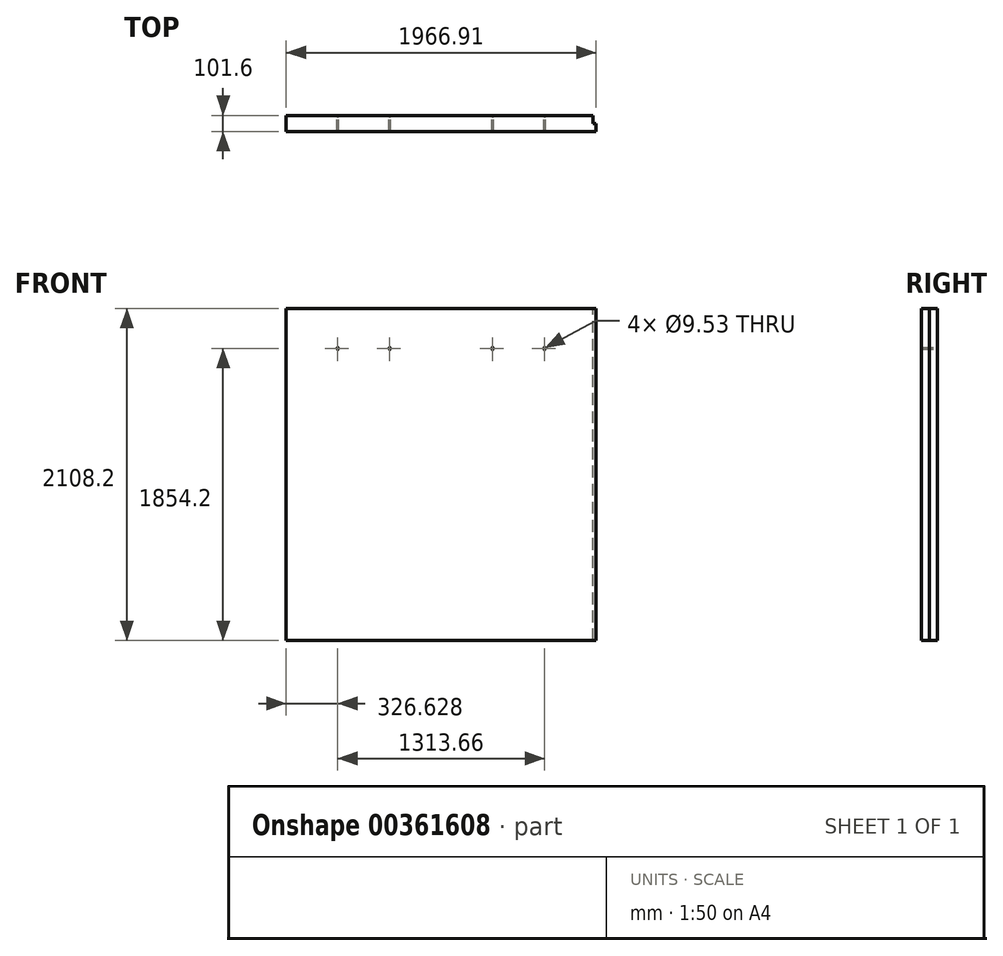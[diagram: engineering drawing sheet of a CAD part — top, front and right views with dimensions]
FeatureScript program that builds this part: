
annotation { "Feature Type Name" : "Feature", "Feature Type Description" : "" }
export const myFeature = defineFeature(function(context is Context, id is Id, definition is map)
    precondition{}
    {
        {
            var Q0;
            Q0=qCreatedBy(makeId("Front.planeOp"),FACE);
            var sketch = newSketch(context, id + "F0", { "sketchPlane" : qUnion([Q0])});
            skLineSegment(sketch, "E0", {"start": v(0, 0) * mm, "end": v(0, 2108.2) * mm});
            skLineSegment(sketch, "E1", {"start": v(0, 2108.2) * mm, "end": v(1966.91, 2108.2) * mm});
            skLineSegment(sketch, "E2", {"start": v(1966.91, 2108.2) * mm, "end": v(1966.91, 0) * mm});
            skLineSegment(sketch, "E3", {"start": v(1966.91, 0) * mm, "end": v(0, 0) * mm});
            skSolve(sketch);
        }
        {
            var Q0;
            Q0=makeQuery(id+"F0.imprint","IMPRINT",FACE,{"disambiguationData":[TD([[makeQuery(id+"F0.imprint","IMPRINT",EDGE,{"derivedFrom":sQuery(id+"F0.wireOp",EDGE,"E0")}),-1.0]])]});
            extrude(context, id + "F1", {"entities" : qUnion([Q0]), "depth" : 101.6 * mm});
        }
        {
            var Q0;
            Q0=makeQuery(id+"F1.opExtrude","SWEPT_FACE",FACE,{"disambiguationData":[OSD([sQuery(id+"F0.wireOp",EDGE,"E1")])]});
            var sketch = newSketch(context, id + "F2", { "sketchPlane" : qUnion([Q0])});
            skLineSegment(sketch, "E4", {"start": v(1966.91, -50.8) * mm, "end": v(1947.86, -50.8) * mm});
            skPoint(sketch, "E4.endSnap0", {"position": v(1966.91, -50.8) * mm});
            skLineSegment(sketch, "E5", {"start": v(1947.86, -50.8) * mm, "end": v(1947.86, 0) * mm});
            skLineSegment(sketch, "E6", {"start": v(1947.86, 0) * mm, "end": v(1966.91, 0) * mm});
            skLineSegment(sketch, "E7", {"start": v(1966.91, 0) * mm, "end": v(1966.91, -50.8) * mm});
            skSolve(sketch);
        }
        {
            var Q0;
            Q0=makeQuery(id+"F2.imprint","IMPRINT",FACE,{"disambiguationData":[TD([[makeQuery(id+"F2.imprint","IMPRINT",EDGE,{"derivedFrom":sQuery(id+"F2.wireOp",EDGE,"E4")}),-1.0]])]});
            extrude(context, id + "F3", {"entities" : qUnion([Q0]), "operationType" : NewBodyOperationType.REMOVE, "endBound" : BoundingType.THROUGH_ALL, "oppositeDirection" : true, "depth" : 25.4 * mm});
        }
        {
            var Q0;
            Q0=makeQuery(id+"F1.opExtrude","CAP_FACE",FACE,{"disambiguationData":[OSD([sQuery(id+"F0.wireOp",EDGE,"E0"),sQuery(id+"F0.wireOp",EDGE,"E1"),sQuery(id+"F0.wireOp",EDGE,"E2"),sQuery(id+"F0.wireOp",EDGE,"E3")])],"isStart":true});
            var sketch = newSketch(context, id + "F4", { "sketchPlane" : qUnion([Q0])});
            skSolve(sketch);
        }
        {
            var Q0;
            Q0=makeQuery(id+"F4.imprint","IMPRINT",FACE,{"disambiguationData":[TD([[makeQuery(id+"F4.imprint","IMPRINT",EDGE,{"derivedFrom":makeQuery(id+"F1.opExtrude","CAP_EDGE",EDGE,{"disambiguationData":[OSD([sQuery(id+"F0.wireOp",EDGE,"E0")])],"isStart":true})}),1.0]])]});
            var sketch = newSketch(context, id + "F5", { "sketchPlane" : qUnion([Q0])});
            skLineSegment(sketch, "E8", {"start": v(-983.46, 2108.2) * mm, "end": v(-983.46, -573.26) * mm, "construction": true});
            skLineSegment(sketch, "E9", {"start": v(-1475.18, 2108.2) * mm, "end": v(-1475.18, 1777.43) * mm, "construction": true});
            skPoint(sketch, "E10", {"position": v(-1640.28, 1854.2) * mm});
            skPoint(sketch, "E11.MirrorP", {"position": v(-1310.08, 1854.2) * mm});
            skLineSegment(sketch, "E12.MirrorCS", {"start": v(-1966.91, 2108.2) * mm, "end": v(-1966.91, -573.26) * mm, "construction": true});
            skPoint(sketch, "E13.MirrorP", {"position": v(-656.83, 1854.2) * mm});
            skPoint(sketch, "E14.MirrorP", {"position": v(-326.63, 1854.2) * mm});
            skSolve(sketch);
        }
        {
            var Q0;
            Q0=sQuery(id+"F5.wireOp",VERTEX,"eac3bd5d-3a7b-4b20-918a-15f79ffad81a");
            var Q1;
            Q1=sQuery(id+"F5.wireOp",VERTEX,"572033d4-c306-406b-9924-44bfefb0f7cb0.MirrorP");
            var Q2;
            Q2=sQuery(id+"F5.wireOp",VERTEX,"8c06a2b8-dc20-44e9-86e1-3b3793f6c89d0.MirrorP");
            var Q3;
            Q3=sQuery(id+"F5.wireOp",VERTEX,"100cf068-bade-4bd2-9d2e-fdefaeea75370.MirrorP");
            var Q4;
            Q4=sQuery(id+"F5.wireOp",VERTEX,"E10");
            var Q5;
            Q5=sQuery(id+"F5.wireOp",VERTEX,"E11.MirrorP");
            var Q6;
            Q6=sQuery(id+"F5.wireOp",VERTEX,"E13.MirrorP");
            var Q7;
            Q7=sQuery(id+"F5.wireOp",VERTEX,"E14.MirrorP");
            var Q8;
            Q8=makeQuery(id+"F1.opExtrude","SWEPT_BODY",BODY,{"disambiguationData":[OSD([sQuery(id+"F0.wireOp",EDGE,"E0"),sQuery(id+"F0.wireOp",EDGE,"E1"),sQuery(id+"F0.wireOp",EDGE,"E2"),sQuery(id+"F0.wireOp",EDGE,"E3")])]});
            hole(context, id + "F6", {"style" : HoleStyle.C_SINK, "endStyle" : HoleEndStyle.THROUGH, "holeDiameter" : 9.52 * mm, "cSinkDiameter" : 19.84 * mm, "cSinkAngle" : 82 * degree, "isTappedThrough" : true, "tappedDepth" : 12.7 * mm, "tapClearance" : 3, "locations" : qUnion([Q0, Q1, Q2, Q3, Q4, Q5, Q6, Q7]), "scope" : qUnion([Q8])});
        }
    });
